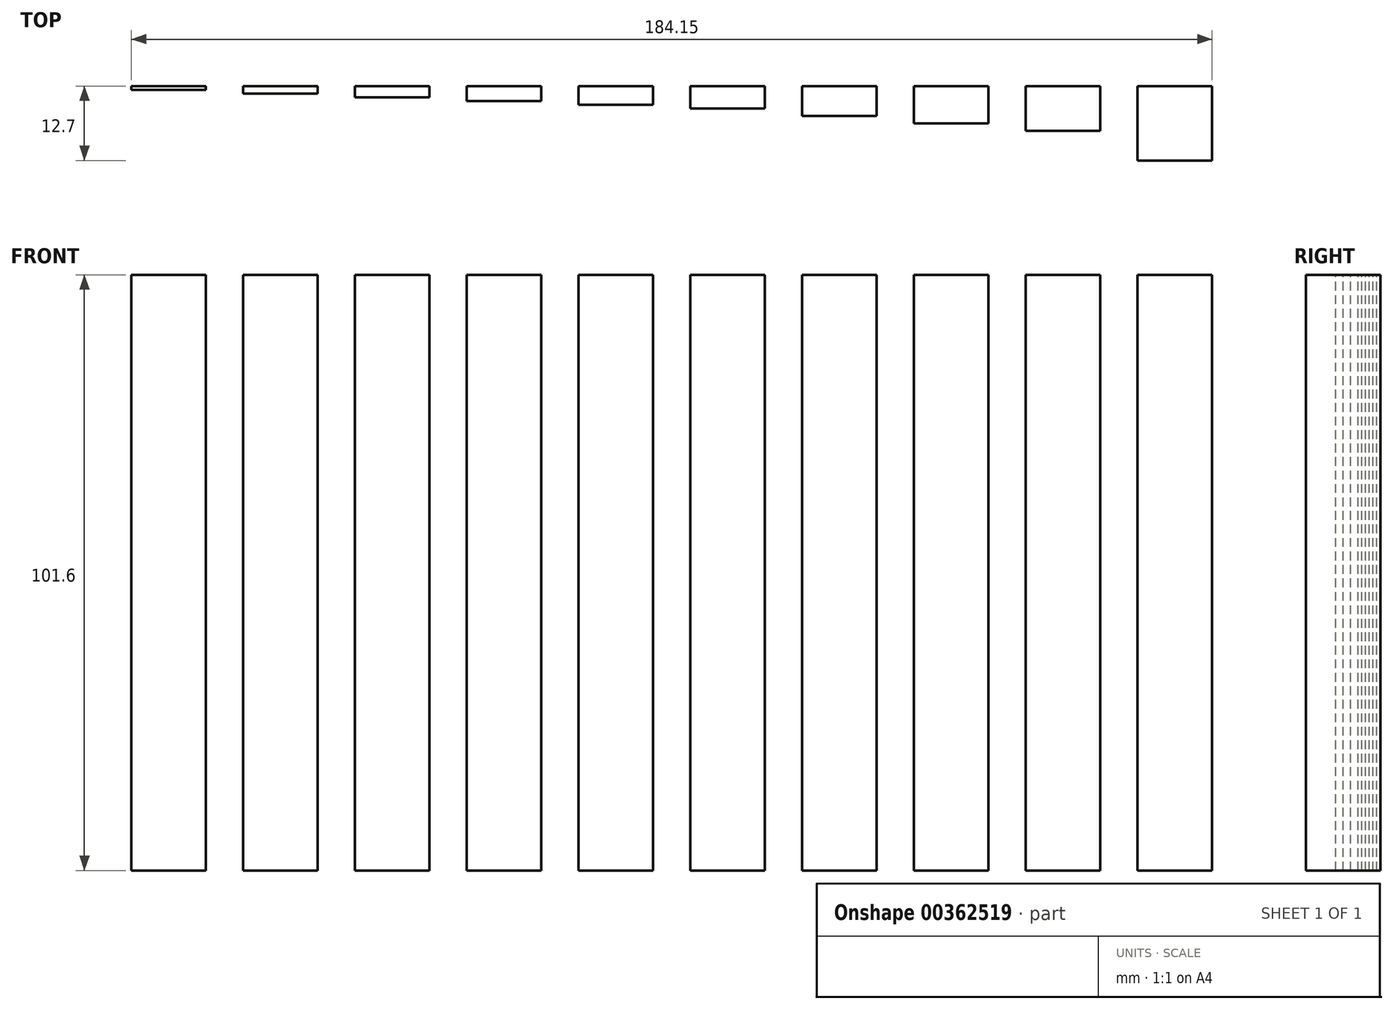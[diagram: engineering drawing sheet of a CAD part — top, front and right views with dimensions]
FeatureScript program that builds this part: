
annotation { "Feature Type Name" : "Feature", "Feature Type Description" : "" }
export const myFeature = defineFeature(function(context is Context, id is Id, definition is map)
    precondition{}
    {
        {
            var Q0;
            Q0=qCreatedBy(makeId("Front.planeOp"),FACE);
            var sketch = newSketch(context, id + "F0", { "sketchPlane" : qUnion([Q0])});
            skLineSegment(sketch, "E0", {"start": v(0, 0) * mm, "end": v(0, 101.6) * mm});
            skLineSegment(sketch, "E1", {"start": v(0, 101.6) * mm, "end": v(12.7, 101.6) * mm});
            skLineSegment(sketch, "E2", {"start": v(12.7, 101.6) * mm, "end": v(12.7, 0) * mm});
            skLineSegment(sketch, "E3", {"start": v(12.7, 0) * mm, "end": v(0, 0) * mm});
            skSolve(sketch);
        }
        {
            var Q0;
            Q0=makeQuery(id+"F0.imprint","IMPRINT",FACE,{"disambiguationData":[TD([[makeQuery(id+"F0.imprint","IMPRINT",EDGE,{"derivedFrom":sQuery(id+"F0.wireOp",EDGE,"E0")}),-1.0]])]});
            extrude(context, id + "F1", {"entities" : qUnion([Q0]), "depth" : 0.64 * mm});
        }
        {
            var Q0;
            Q0=qCreatedBy(makeId("Front.planeOp"),FACE);
            var sketch = newSketch(context, id + "F2", { "sketchPlane" : qUnion([Q0])});
            skLineSegment(sketch, "E4", {"start": v(19.05, 0) * mm, "end": v(19.05, 101.6) * mm});
            skLineSegment(sketch, "E5", {"start": v(19.05, 101.6) * mm, "end": v(31.75, 101.6) * mm});
            skLineSegment(sketch, "E6", {"start": v(31.75, 101.6) * mm, "end": v(31.75, 0) * mm});
            skLineSegment(sketch, "E7", {"start": v(31.75, 0) * mm, "end": v(19.05, 0) * mm});
            skSolve(sketch);
        }
        {
            var Q0;
            Q0 = qSketchRegion(id + "F2", true);
            extrude(context, id + "F3", {"entities" : qUnion([Q0]), "depth" : 1.27 * mm});
        }
        {
            var Q0;
            Q0=qCreatedBy(makeId("Front.planeOp"),FACE);
            var sketch = newSketch(context, id + "F4", { "sketchPlane" : qUnion([Q0])});
            skLineSegment(sketch, "E8.bottom", {"start": v(38.1, 0) * mm, "end": v(50.8, 0) * mm});
            skLineSegment(sketch, "E8.top", {"start": v(38.1, 101.6) * mm, "end": v(50.8, 101.6) * mm});
            skLineSegment(sketch, "E8.left", {"start": v(38.1, 0) * mm, "end": v(38.1, 101.6) * mm});
            skLineSegment(sketch, "E8.right", {"start": v(50.8, 0) * mm, "end": v(50.8, 101.6) * mm});
            skSolve(sketch);
        }
        {
            var Q0;
            Q0=makeQuery(id+"F4.imprint","IMPRINT",FACE,{"disambiguationData":[TD([[makeQuery(id+"F4.imprint","IMPRINT",EDGE,{"derivedFrom":sQuery(id+"F4.wireOp",EDGE,"E8.bottom")}),1.0]])]});
            extrude(context, id + "F5", {"entities" : qUnion([Q0]), "depth" : 1.9 * mm});
        }
        {
            var Q0;
            Q0=qCreatedBy(makeId("Front.planeOp"),FACE);
            var sketch = newSketch(context, id + "F6", { "sketchPlane" : qUnion([Q0])});
            skLineSegment(sketch, "E9.bottom", {"start": v(57.15, 0) * mm, "end": v(69.85, 0) * mm});
            skLineSegment(sketch, "E9.top", {"start": v(57.15, 101.6) * mm, "end": v(69.85, 101.6) * mm});
            skLineSegment(sketch, "E9.left", {"start": v(57.15, 0) * mm, "end": v(57.15, 101.6) * mm});
            skLineSegment(sketch, "E9.right", {"start": v(69.85, 0) * mm, "end": v(69.85, 101.6) * mm});
            skSolve(sketch);
        }
        {
            var Q0;
            Q0 = qSketchRegion(id + "F6", true);
            extrude(context, id + "F7", {"entities" : qUnion([Q0]), "depth" : 2.54 * mm});
        }
        {
            var Q0;
            Q0=qCreatedBy(makeId("Front.planeOp"),FACE);
            var sketch = newSketch(context, id + "F8", { "sketchPlane" : qUnion([Q0])});
            skLineSegment(sketch, "E10.bottom", {"start": v(76.2, 0) * mm, "end": v(88.9, 0) * mm});
            skLineSegment(sketch, "E10.top", {"start": v(76.2, 101.6) * mm, "end": v(88.9, 101.6) * mm});
            skLineSegment(sketch, "E10.left", {"start": v(76.2, 0) * mm, "end": v(76.2, 101.6) * mm});
            skLineSegment(sketch, "E10.right", {"start": v(88.9, 0) * mm, "end": v(88.9, 101.6) * mm});
            skSolve(sketch);
        }
        {
            var Q0;
            Q0 = qSketchRegion(id + "F8", true);
            extrude(context, id + "F9", {"entities" : qUnion([Q0]), "depth" : 3.17 * mm});
        }
        {
            var Q0;
            Q0=qCreatedBy(makeId("Front.planeOp"),FACE);
            var sketch = newSketch(context, id + "F10", { "sketchPlane" : qUnion([Q0])});
            skLineSegment(sketch, "E11.bottom", {"start": v(95.25, 0) * mm, "end": v(107.95, 0) * mm});
            skLineSegment(sketch, "E11.top", {"start": v(95.25, 101.6) * mm, "end": v(107.95, 101.6) * mm});
            skLineSegment(sketch, "E11.left", {"start": v(95.25, 0) * mm, "end": v(95.25, 101.6) * mm});
            skLineSegment(sketch, "E11.right", {"start": v(107.95, 0) * mm, "end": v(107.95, 101.6) * mm});
            skSolve(sketch);
        }
        {
            var Q0;
            Q0 = qSketchRegion(id + "F10", true);
            extrude(context, id + "F11", {"entities" : qUnion([Q0]), "depth" : 3.8 * mm});
        }
        {
            var Q0;
            Q0=qCreatedBy(makeId("Front.planeOp"),FACE);
            var sketch = newSketch(context, id + "F12", { "sketchPlane" : qUnion([Q0])});
            skLineSegment(sketch, "E12.bottom", {"start": v(114.3, 0) * mm, "end": v(127, 0) * mm});
            skLineSegment(sketch, "E12.top", {"start": v(114.3, 101.6) * mm, "end": v(127, 101.6) * mm});
            skLineSegment(sketch, "E12.left", {"start": v(114.3, 0) * mm, "end": v(114.3, 101.6) * mm});
            skLineSegment(sketch, "E12.right", {"start": v(127, 0) * mm, "end": v(127, 101.6) * mm});
            skSolve(sketch);
        }
        {
            var Q0;
            Q0 = qSketchRegion(id + "F12", true);
            extrude(context, id + "F13", {"entities" : qUnion([Q0]), "depth" : 5.08 * mm});
        }
        {
            var Q0;
            Q0=qCreatedBy(makeId("Front.planeOp"),FACE);
            var sketch = newSketch(context, id + "F14", { "sketchPlane" : qUnion([Q0])});
            skLineSegment(sketch, "E13.bottom", {"start": v(133.35, 0) * mm, "end": v(146.05, 0) * mm});
            skLineSegment(sketch, "E13.top", {"start": v(133.35, 101.6) * mm, "end": v(146.05, 101.6) * mm});
            skLineSegment(sketch, "E13.left", {"start": v(133.35, 0) * mm, "end": v(133.35, 101.6) * mm});
            skLineSegment(sketch, "E13.right", {"start": v(146.05, 0) * mm, "end": v(146.05, 101.6) * mm});
            skSolve(sketch);
        }
        {
            var Q0;
            Q0 = qSketchRegion(id + "F14", true);
            extrude(context, id + "F15", {"entities" : qUnion([Q0]), "depth" : 6.35 * mm});
        }
        {
            var Q0;
            Q0=qCreatedBy(makeId("Front.planeOp"),FACE);
            var sketch = newSketch(context, id + "F16", { "sketchPlane" : qUnion([Q0])});
            skLineSegment(sketch, "E14.bottom", {"start": v(152.4, 0) * mm, "end": v(165.1, 0) * mm});
            skLineSegment(sketch, "E14.top", {"start": v(152.4, 101.6) * mm, "end": v(165.1, 101.6) * mm});
            skLineSegment(sketch, "E14.left", {"start": v(152.4, 0) * mm, "end": v(152.4, 101.6) * mm});
            skLineSegment(sketch, "E14.right", {"start": v(165.1, 0) * mm, "end": v(165.1, 101.6) * mm});
            skSolve(sketch);
        }
        {
            var Q0;
            Q0 = qSketchRegion(id + "F16", true);
            extrude(context, id + "F17", {"entities" : qUnion([Q0]), "depth" : 7.62 * mm});
        }
        {
            var Q0;
            Q0=qCreatedBy(makeId("Front.planeOp"),FACE);
            var sketch = newSketch(context, id + "F18", { "sketchPlane" : qUnion([Q0])});
            skLineSegment(sketch, "E15.bottom", {"start": v(171.45, 0) * mm, "end": v(184.15, 0) * mm});
            skLineSegment(sketch, "E15.top", {"start": v(171.45, 101.6) * mm, "end": v(184.15, 101.6) * mm});
            skLineSegment(sketch, "E15.left", {"start": v(171.45, 0) * mm, "end": v(171.45, 101.6) * mm});
            skLineSegment(sketch, "E15.right", {"start": v(184.15, 0) * mm, "end": v(184.15, 101.6) * mm});
            skSolve(sketch);
        }
        {
            var Q0;
            Q0 = qSketchRegion(id + "F18", true);
            extrude(context, id + "F19", {"entities" : qUnion([Q0]), "depth" : 12.7 * mm});
        }
    });
